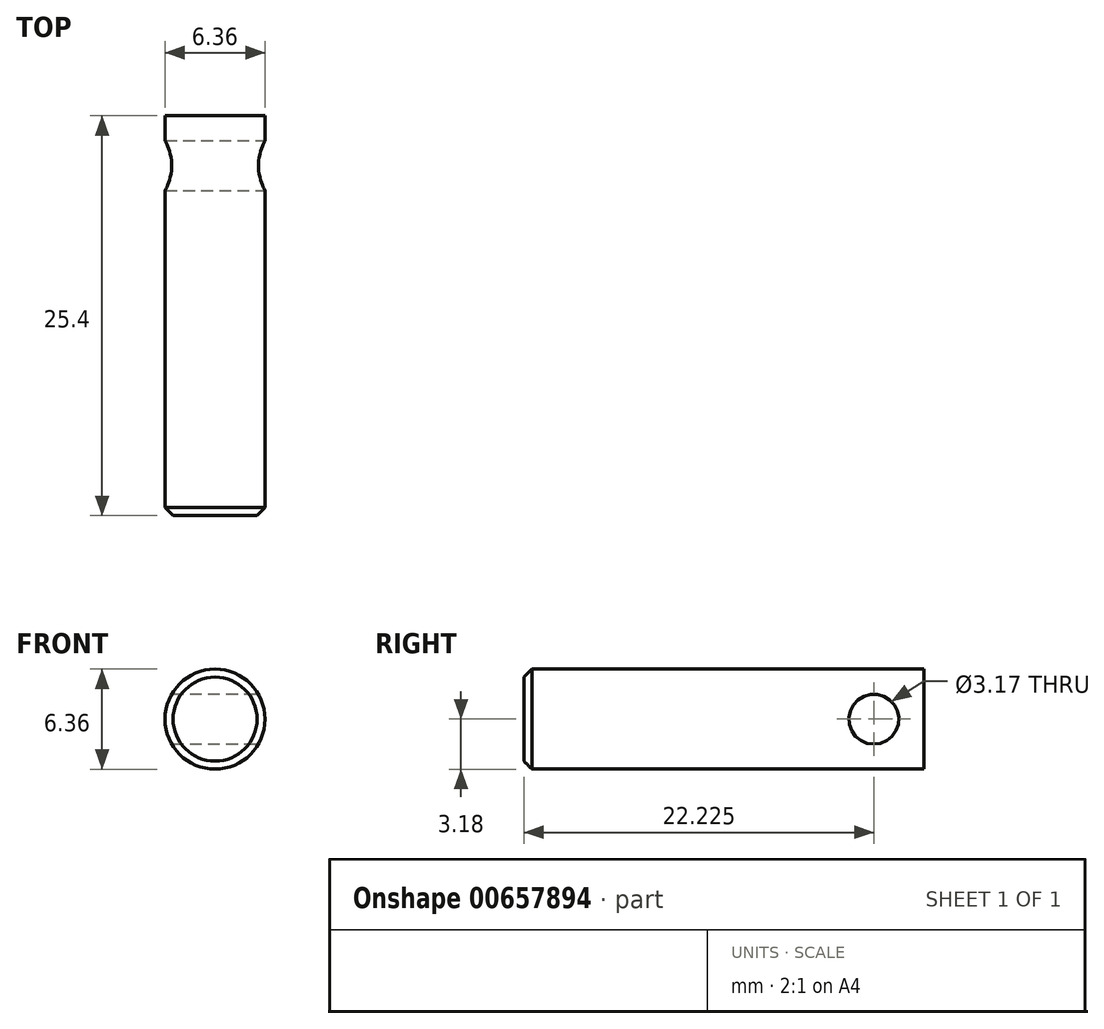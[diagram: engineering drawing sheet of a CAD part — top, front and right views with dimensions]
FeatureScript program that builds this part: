
annotation { "Feature Type Name" : "Feature", "Feature Type Description" : "" }
export const myFeature = defineFeature(function(context is Context, id is Id, definition is map)
    precondition{}
    {
        {
            var Q0;
            Q0=qCreatedBy(makeId("Front.planeOp"),FACE);
            var sketch = newSketch(context, id + "F0", { "sketchPlane" : qUnion([Q0])});
            skCircle(sketch, "E0", {"center": v(0, 0) * mm, "radius": 3.18 * mm});
            skSolve(sketch);
        }
        {
            var Q0;
            Q0 = qSketchRegion(id + "F0", true);
            extrude(context, id + "F1", {"entities" : qUnion([Q0]), "depth" : 25.4 * mm, "offsetDistance" : 25.4 * mm});
        }
        {
            var Q0;
            Q0=makeQuery(id+"F1.opExtrude","CAP_EDGE",EDGE,{"disambiguationData":[OSD([sQuery(id+"F0.wireOp",EDGE,"E0")])],"isStart":false});
            chamfer(context, id + "F2", {"entities" : qUnion([Q0]), "width" : 0.5 * mm, "tangentPropagation" : true});
        }
        {
            var Q0;
            Q0=qCreatedBy(makeId("Right.planeOp"),FACE);
            var sketch = newSketch(context, id + "F3", { "sketchPlane" : qUnion([Q0])});
            skCircle(sketch, "E1", {"center": v(-3.18, 0) * mm, "radius": 1.59 * mm});
            skSolve(sketch);
        }
        {
            var Q0;
            Q0 = qSketchRegion(id + "F3", true);
            extrude(context, id + "F4", {"entities" : qUnion([Q0]), "operationType" : NewBodyOperationType.REMOVE, "endBound" : BoundingType.SYMMETRIC, "oppositeDirection" : true, "depth" : 6.35 * mm, "offsetDistance" : 25.4 * mm});
        }
    });
